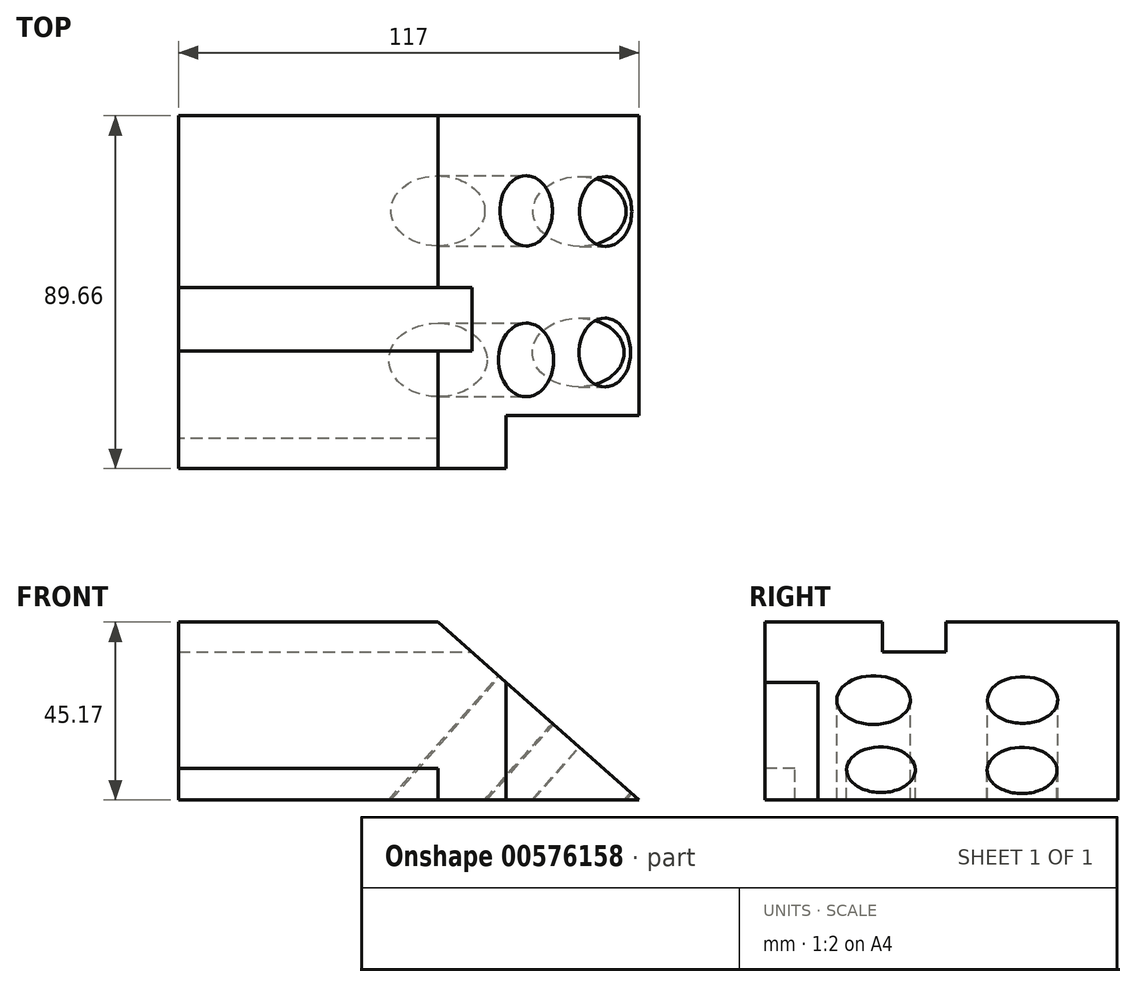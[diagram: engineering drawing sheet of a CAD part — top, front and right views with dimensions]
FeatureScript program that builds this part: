
annotation { "Feature Type Name" : "Feature", "Feature Type Description" : "" }
export const myFeature = defineFeature(function(context is Context, id is Id, definition is map)
    precondition{}
    {
        {
            var Q0;
            Q0=qCreatedBy(makeId("Front.planeOp"),FACE);
            var sketch = newSketch(context, id + "F0", { "sketchPlane" : qUnion([Q0])});
            skLineSegment(sketch, "E0.bottom", {"start": v(0, 0) * mm, "end": v(-65.92, 0) * mm});
            skLineSegment(sketch, "E0.top", {"start": v(0, 45.17) * mm, "end": v(-65.92, 45.17) * mm});
            skLineSegment(sketch, "E0.left", {"start": v(0, 0) * mm, "end": v(0, 45.17) * mm});
            skLineSegment(sketch, "E0.right", {"start": v(-65.92, 0) * mm, "end": v(-65.92, 45.17) * mm});
            skLineSegment(sketch, "E1", {"start": v(0, 45.17) * mm, "end": v(51.08, 0) * mm});
            skLineSegment(sketch, "E2", {"start": v(51.08, 0) * mm, "end": v(0, 0) * mm});
            skSolve(sketch);
        }
        {
            var Q0;
            Q0 = qSketchRegion(id + "F0", true);
            extrude(context, id + "F1", {"entities" : qUnion([Q0]), "depth" : 76.2 * mm, "offsetDistance" : 25.4 * mm});
        }
        {
            var Q0;
            Q0=makeQuery(id+"F1.opExtrude","SWEPT_FACE",FACE,{"disambiguationData":[OSD([sQuery(id+"F0.wireOp",EDGE,"E0.top")])]});
            var sketch = newSketch(context, id + "F2", { "sketchPlane" : qUnion([Q0])});
            skLineSegment(sketch, "E3.bottom", {"start": v(-65.92, -43.71) * mm, "end": v(0, -43.71) * mm});
            skLineSegment(sketch, "E3.top", {"start": v(-65.92, -59.84) * mm, "end": v(0, -59.84) * mm});
            skLineSegment(sketch, "E3.left", {"start": v(-65.92, -43.71) * mm, "end": v(-65.92, -59.84) * mm});
            skLineSegment(sketch, "E3.right", {"start": v(0, -43.71) * mm, "end": v(0, -59.84) * mm});
            skSolve(sketch);
        }
        {
            var Q0;
            Q0 = qSketchRegion(id + "F2", true);
            extrude(context, id + "F3", {"entities" : qUnion([Q0]), "operationType" : NewBodyOperationType.REMOVE, "oppositeDirection" : true, "depth" : 7.62 * mm, "offsetDistance" : 25.4 * mm});
        }
        {
            var Q0;
            Q0=makeQuery(id+"F1.opExtrude","CAP_FACE",FACE,{"disambiguationData":[OSD([sQuery(id+"F0.wireOp",EDGE,"E0.bottom"),sQuery(id+"F0.wireOp",EDGE,"E0.top"),sQuery(id+"F0.wireOp",EDGE,"E0.right"),sQuery(id+"F0.wireOp",EDGE,"E1"),sQuery(id+"F0.wireOp",EDGE,"E2")])],"isStart":false});
            var sketch = newSketch(context, id + "F4", { "sketchPlane" : qUnion([Q0])});
            skLineSegment(sketch, "E4", {"start": v(17.3, 29.87) * mm, "end": v(17.3, 0) * mm});
            skLineSegment(sketch, "E5", {"start": v(17.3, 0) * mm, "end": v(-14.3, 0) * mm});
            skLineSegment(sketch, "E6", {"start": v(-14.3, 0) * mm, "end": v(-14.3, 45.17) * mm});
            skLineSegment(sketch, "E7", {"start": v(-14.3, 45.17) * mm, "end": v(0, 45.17) * mm});
            skLineSegment(sketch, "E8", {"start": v(0, 45.17) * mm, "end": v(17.3, 29.87) * mm});
            skSolve(sketch);
        }
        {
            var Q0;
            Q0 = qSketchRegion(id + "F4", true);
            extrude(context, id + "F5", {"entities" : qUnion([Q0]), "operationType" : NewBodyOperationType.ADD, "depth" : 13.46 * mm, "offsetDistance" : 25.4 * mm});
        }
        {
            var Q0;
            {var subQ0=sQuery(id+"F0.wireOp",EDGE,"E0.top");var subQ1=sQuery(id+"F0.wireOp",EDGE,"E0.right");var subQ2=sQuery(id+"F0.wireOp",EDGE,"E2");var subQ3=sQuery(id+"F0.wireOp",EDGE,"E0.bottom");Q0=makeQuery(id+"F5.boolean.opBoolean","SPLIT",FACE,{"disambiguationData":[TD([makeQuery(id+"F1.opExtrude","SWEPT_FACE",FACE,{"disambiguationData":[OSD([subQ0])]})])],"derivedFrom":makeQuery(id+"F1.opExtrude","CAP_FACE",FACE,{"disambiguationData":[OSD([subQ3,subQ0,subQ1,sQuery(id+"F0.wireOp",EDGE,"E1"),subQ2])],"isStart":false})});}
            var sketch = newSketch(context, id + "F6", { "sketchPlane" : qUnion([Q0])});
            skLineSegment(sketch, "E9", {"start": v(-65.92, 45.17) * mm, "end": v(-14.3, 45.17) * mm});
            skLineSegment(sketch, "E10", {"start": v(-14.3, 45.17) * mm, "end": v(-14.3, 0) * mm});
            skLineSegment(sketch, "E11", {"start": v(-14.3, 0) * mm, "end": v(-65.92, 0) * mm});
            skLineSegment(sketch, "E12", {"start": v(-65.92, 0) * mm, "end": v(-65.92, 45.17) * mm});
            skSolve(sketch);
        }
        {
            var Q0;
            Q0 = qSketchRegion(id + "F6", true);
            extrude(context, id + "F7", {"entities" : qUnion([Q0]), "operationType" : NewBodyOperationType.ADD, "depth" : 13.46 * mm, "offsetDistance" : 25.4 * mm});
        }
        {
            var Q0;
            Q0=makeQuery(id+"F7.boolean.opBoolean","MERGE",FACE,{"derivedFrom":[makeQuery(id+"F5.opExtrude","CAP_FACE",FACE,{"disambiguationData":[OSD([sQuery(id+"F4.wireOp",EDGE,"E4"),sQuery(id+"F4.wireOp",EDGE,"E5"),sQuery(id+"F4.wireOp",EDGE,"E6"),sQuery(id+"F4.wireOp",EDGE,"E7"),sQuery(id+"F4.wireOp",EDGE,"E8")])],"isStart":false}),makeQuery(id+"F7.opExtrude","CAP_FACE",FACE,{"disambiguationData":[OSD([sQuery(id+"F6.wireOp",EDGE,"E9"),sQuery(id+"F6.wireOp",EDGE,"E10"),sQuery(id+"F6.wireOp",EDGE,"E11"),sQuery(id+"F6.wireOp",EDGE,"E12")])],"isStart":false})]});
            var sketch = newSketch(context, id + "F8", { "sketchPlane" : qUnion([Q0])});
            skLineSegment(sketch, "E13.bottom", {"start": v(-65.92, 0) * mm, "end": v(0, 0) * mm});
            skLineSegment(sketch, "E13.top", {"start": v(-65.92, 7.96) * mm, "end": v(0, 7.96) * mm});
            skLineSegment(sketch, "E13.left", {"start": v(-65.92, 0) * mm, "end": v(-65.92, 7.96) * mm});
            skLineSegment(sketch, "E13.right", {"start": v(0, 0) * mm, "end": v(0, 7.96) * mm});
            skSolve(sketch);
        }
        {
            var Q0;
            Q0=makeQuery(id+"F8.imprint","IMPRINT",FACE,{"disambiguationData":[TD([[makeQuery(id+"F8.imprint","IMPRINT",EDGE,{"derivedFrom":sQuery(id+"F8.wireOp",EDGE,"E13.bottom")}),-1.0]])]});
            extrude(context, id + "F9", {"entities" : qUnion([Q0]), "operationType" : NewBodyOperationType.REMOVE, "oppositeDirection" : true, "depth" : 7.62 * mm, "offsetDistance" : 25.4 * mm});
        }
        {
            var Q0;
            Q0=makeQuery(id+"F3.boolean.opBoolean","COPY",FACE,{"derivedFrom":makeQuery(id+"F3.opExtrude","SWEPT_FACE",FACE,{"disambiguationData":[OSD([sQuery(id+"F2.wireOp",EDGE,"E3.right")])]})});
            extrude(context, id + "F10", {"entities" : qUnion([Q0]), "operationType" : NewBodyOperationType.REMOVE, "oppositeDirection" : true, "depth" : 25.4 * mm, "offsetDistance" : 25.4 * mm});
        }
        {
            var Q0;
            Q0=makeQuery(id+"F5.boolean.opBoolean","MERGE",FACE,{"derivedFrom":[makeQuery(id+"F1.opExtrude","SWEPT_FACE",FACE,{"disambiguationData":[OSD([sQuery(id+"F0.wireOp",EDGE,"E1")])]}),makeQuery(id+"F5.opExtrude","SWEPT_FACE",FACE,{"disambiguationData":[OSD([sQuery(id+"F4.wireOp",EDGE,"E8")])]})]});
            var sketch = newSketch(context, id + "F11", { "sketchPlane" : qUnion([Q0])});
            skCircle(sketch, "E14", {"center": v(0, -62.04) * mm, "radius": 9.34 * mm});
            skCircle(sketch, "E15", {"center": v(26.72, -60.17) * mm, "radius": 8.73 * mm});
            skCircle(sketch, "E16", {"center": v(0, -24.2) * mm, "radius": 8.92 * mm});
            skCircle(sketch, "E17", {"center": v(26.97, -24.33) * mm, "radius": 8.87 * mm});
            skSolve(sketch);
        }
        {
            var Q0;
            Q0 = qSketchRegion(id + "F11", true);
            extrude(context, id + "F12", {"entities" : qUnion([Q0]), "operationType" : NewBodyOperationType.REMOVE, "oppositeDirection" : true, "depth" : 88.65 * mm, "offsetDistance" : 25.4 * mm});
        }
    });
